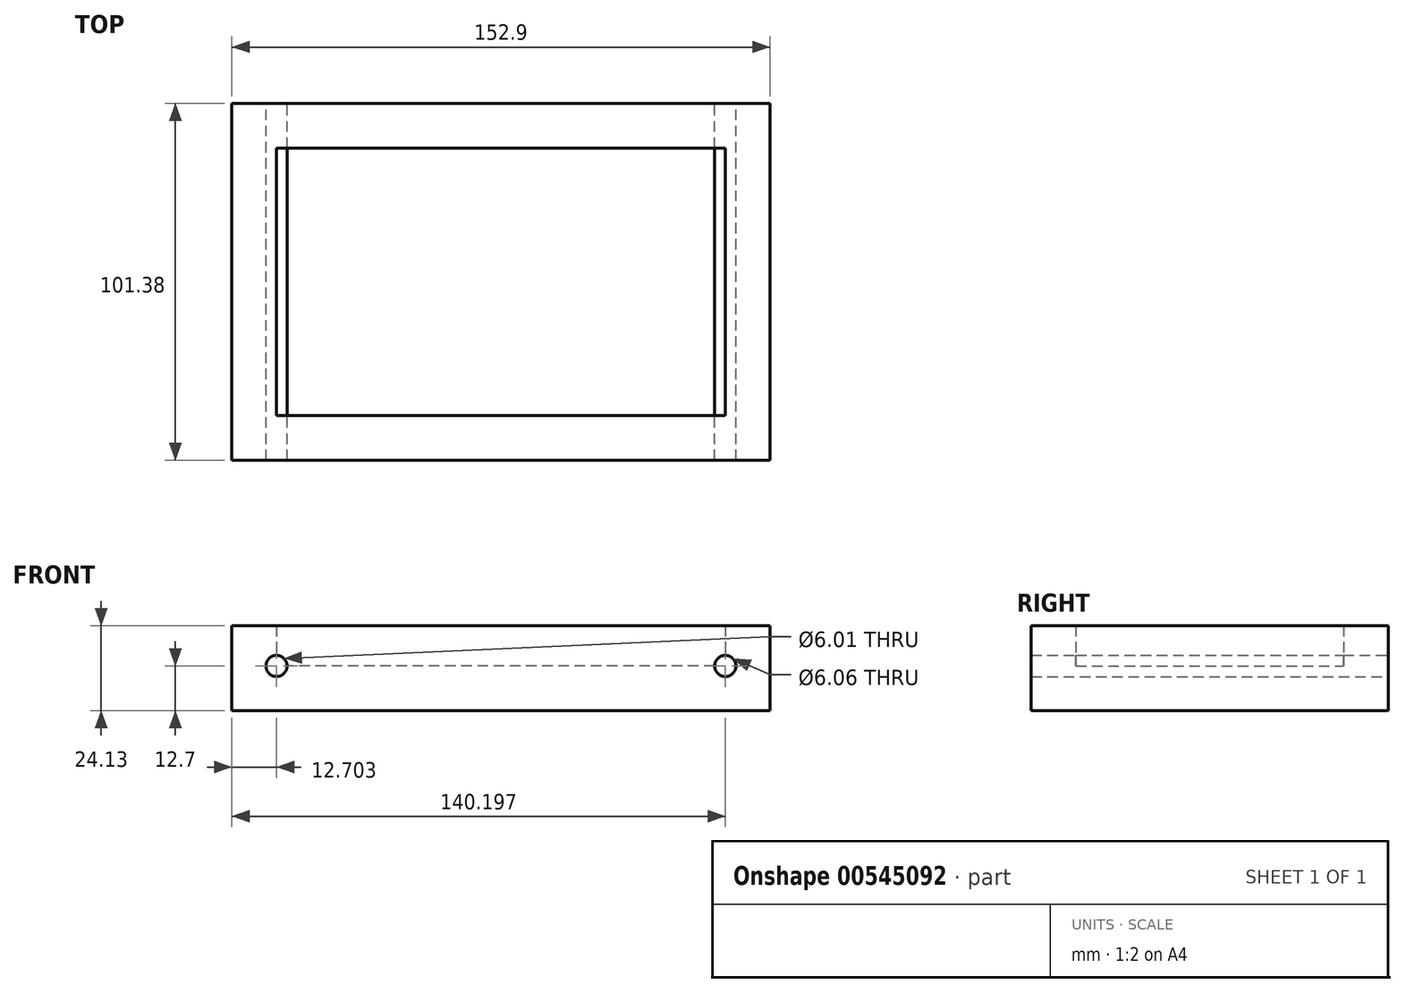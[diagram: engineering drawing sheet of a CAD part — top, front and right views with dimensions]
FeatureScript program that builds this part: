
annotation { "Feature Type Name" : "Feature", "Feature Type Description" : "" }
export const myFeature = defineFeature(function(context is Context, id is Id, definition is map)
    precondition{}
    {
        {
            var Q0;
            Q0=qCreatedBy(makeId("Top.planeOp"),FACE);
            var sketch = newSketch(context, id + "F0", { "sketchPlane" : qUnion([Q0])});
            skLineSegment(sketch, "E0.bottom", {"start": v(76.45, 50.7) * mm, "end": v(-76.45, 50.7) * mm});
            skLineSegment(sketch, "E0.top", {"start": v(76.45, -50.7) * mm, "end": v(-76.45, -50.7) * mm});
            skLineSegment(sketch, "E0.left", {"start": v(76.45, 50.7) * mm, "end": v(76.45, -50.7) * mm});
            skLineSegment(sketch, "E0.right", {"start": v(-76.45, 50.7) * mm, "end": v(-76.45, -50.7) * mm});
            skPoint(sketch, "E0.middle", {"position": v(0, 0) * mm});
            skSolve(sketch);
        }
        {
            var Q0;
            Q0 = qSketchRegion(id + "F0", true);
            extrude(context, id + "F1", {"entities" : qUnion([Q0]), "depth" : 24.13 * mm, "offsetDistance" : 25.4 * mm});
        }
        {
            var Q0;
            Q0=makeQuery(id+"F1.opExtrude","CAP_FACE",FACE,{"disambiguationData":[OSD([sQuery(id+"F0.wireOp",EDGE,"E0.bottom"),sQuery(id+"F0.wireOp",EDGE,"E0.top"),sQuery(id+"F0.wireOp",EDGE,"E0.left"),sQuery(id+"F0.wireOp",EDGE,"E0.right")])],"isStart":false});
            shell(context, id + "F2", {"entities" : qUnion([Q0]), "thickness" : 12.7 * mm});
        }
        {
            var Q0;
            Q0=makeQuery(id+"F1.opExtrude","SWEPT_FACE",FACE,{"disambiguationData":[OSD([sQuery(id+"F0.wireOp",EDGE,"E0.bottom")])]});
            var sketch = newSketch(context, id + "F3", { "sketchPlane" : qUnion([Q0])});
            skCircle(sketch, "E1", {"center": v(-63.75, 12.7) * mm, "radius": 3.03 * mm});
            skCircle(sketch, "E2", {"center": v(63.75, 12.7) * mm, "radius": 3 * mm});
            skSolve(sketch);
        }
        {
            var Q0;
            Q0=makeQuery(id+"F3.imprint","IMPRINT",FACE,{"disambiguationData":[TD([[makeQuery(id+"F3.imprint","IMPRINT",EDGE,{"derivedFrom":sQuery(id+"F3.wireOp",EDGE,"E1")}),1.0]])]});
            var Q1;
            Q1=makeQuery(id+"F3.imprint","IMPRINT",FACE,{"disambiguationData":[TD([[makeQuery(id+"F3.imprint","IMPRINT",EDGE,{"derivedFrom":sQuery(id+"F3.wireOp",EDGE,"E2")}),1.0]])]});
            var Q2;
            Q2=makeQuery(id+"F1.opExtrude","SWEPT_FACE",FACE,{"disambiguationData":[OSD([sQuery(id+"F0.wireOp",EDGE,"E0.top")])]});
            extrude(context, id + "F4", {"entities" : qUnion([Q0, Q1]), "operationType" : NewBodyOperationType.REMOVE, "endBound" : BoundingType.UP_TO_SURFACE, "oppositeDirection" : true, "depth" : 25.4 * mm, "endBoundEntityFace" : qUnion([Q2]), "offsetDistance" : 25.4 * mm});
        }
    });
